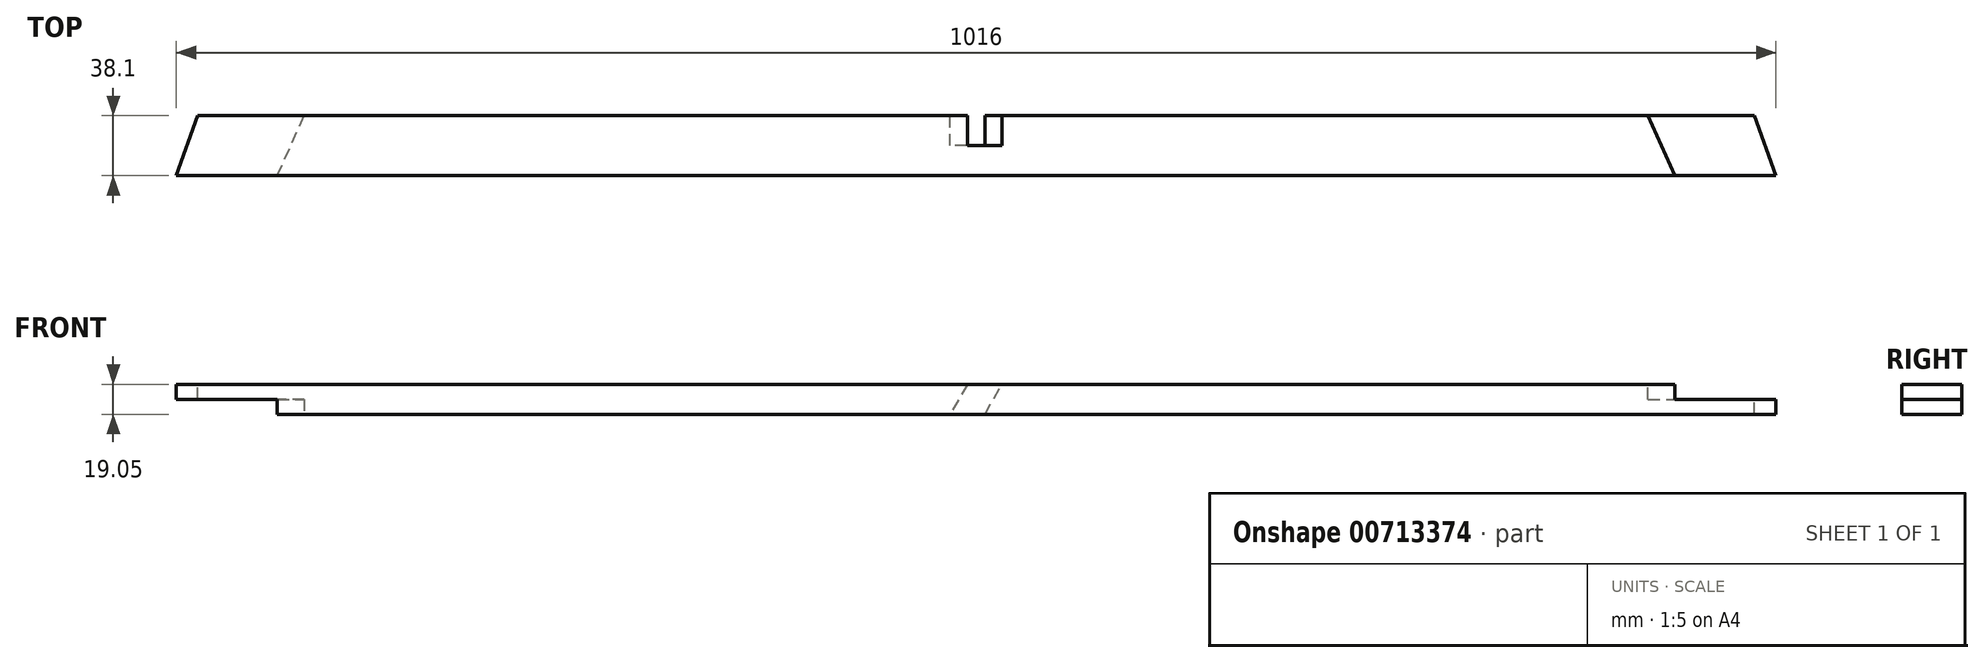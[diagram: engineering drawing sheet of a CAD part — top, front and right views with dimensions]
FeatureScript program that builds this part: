
annotation { "Feature Type Name" : "Feature", "Feature Type Description" : "" }
export const myFeature = defineFeature(function(context is Context, id is Id, definition is map)
    precondition{}
    {
        {
            var Q0;
            Q0=qCreatedBy(makeId("Front.planeOp"),FACE);
            var sketch = newSketch(context, id + "F0", { "sketchPlane" : qUnion([Q0])});
            skLineSegment(sketch, "E0.bottom", {"start": v(0, 0) * mm, "end": v(-1016, 0) * mm});
            skLineSegment(sketch, "E0.top", {"start": v(0, 19.05) * mm, "end": v(-1016, 19.05) * mm});
            skLineSegment(sketch, "E0.left", {"start": v(0, 0) * mm, "end": v(0, 19.05) * mm});
            skLineSegment(sketch, "E0.right", {"start": v(-1016, 0) * mm, "end": v(-1016, 19.05) * mm});
            skSolve(sketch);
        }
        {
            var Q0;
            Q0 = qSketchRegion(id + "F0", true);
            extrude(context, id + "F1", {"entities" : qUnion([Q0]), "depth" : 38.1 * mm, "offsetDistance" : 25.4 * mm});
        }
        {
            var Q0;
            Q0=makeQuery(id+"F1.opExtrude","SWEPT_FACE",FACE,{"disambiguationData":[OSD([sQuery(id+"F0.wireOp",EDGE,"E0.top")])]});
            var sketch = newSketch(context, id + "F2", { "sketchPlane" : qUnion([Q0])});
            skLineSegment(sketch, "E1", {"start": v(-1016, -38.1) * mm, "end": v(-1002.38, 0) * mm});
            skLineSegment(sketch, "E2", {"start": v(-1002.38, 0) * mm, "end": v(-1016, 0) * mm});
            skLineSegment(sketch, "E3", {"start": v(-1016, 0) * mm, "end": v(-1016, -38.1) * mm});
            skSolve(sketch);
        }
        {
            var Q0;
            Q0 = qSketchRegion(id + "F2", true);
            extrude(context, id + "F3", {"entities" : qUnion([Q0]), "operationType" : NewBodyOperationType.REMOVE, "oppositeDirection" : true, "depth" : 50.8 * mm, "offsetDistance" : 25.4 * mm});
        }
        {
            var Q0;
            Q0=makeQuery(id+"F1.opExtrude","SWEPT_FACE",FACE,{"disambiguationData":[OSD([sQuery(id+"F0.wireOp",EDGE,"E0.top")])]});
            var sketch = newSketch(context, id + "F4", { "sketchPlane" : qUnion([Q0])});
            skLineSegment(sketch, "E4", {"start": v(0, -38.1) * mm, "end": v(-13.62, 0) * mm});
            skLineSegment(sketch, "E5", {"start": v(-13.62, 0) * mm, "end": v(0, 0) * mm});
            skLineSegment(sketch, "E6", {"start": v(0, 0) * mm, "end": v(0, -38.1) * mm});
            skSolve(sketch);
        }
        {
            var Q0;
            Q0 = qSketchRegion(id + "F4", true);
            extrude(context, id + "F5", {"entities" : qUnion([Q0]), "operationType" : NewBodyOperationType.REMOVE, "oppositeDirection" : true, "depth" : 76.2 * mm, "offsetDistance" : 25.4 * mm});
        }
        {
            var Q0;
            Q0=makeQuery(id+"F3.boolean.opBoolean","COPY",FACE,{"derivedFrom":makeQuery(id+"F3.opExtrude","SWEPT_FACE",FACE,{"disambiguationData":[OSD([sQuery(id+"F2.wireOp",EDGE,"E1")])]})});
            var sketch = newSketch(context, id + "F6", { "sketchPlane" : qUnion([Q0])});
            skLineSegment(sketch, "E7", {"start": v(258.73, 0) * mm, "end": v(377.94, 0) * mm});
            skLineSegment(sketch, "E8", {"start": v(377.94, 9.53) * mm, "end": v(377.94, 0) * mm});
            skLineSegment(sketch, "E9", {"start": v(377.94, 0) * mm, "end": v(377.94, 9.53) * mm, "construction": true});
            skLineSegment(sketch, "E10", {"start": v(377.94, 9.53) * mm, "end": v(252.78, 9.53) * mm});
            skLineSegment(sketch, "E11", {"start": v(258.73, 0) * mm, "end": v(252.78, 9.53) * mm});
            skSolve(sketch);
        }
        {
            var Q0;
            Q0 = qSketchRegion(id + "F6", true);
            extrude(context, id + "F7", {"entities" : qUnion([Q0]), "operationType" : NewBodyOperationType.REMOVE, "oppositeDirection" : true, "depth" : 60.32 * mm, "offsetDistance" : 25.4 * mm});
        }
        {
            var Q0;
            Q0=makeQuery(id+"F1.opExtrude","SWEPT_FACE",FACE,{"disambiguationData":[OSD([sQuery(id+"F0.wireOp",EDGE,"E0.bottom")])]});
            var sketch = newSketch(context, id + "F8", { "sketchPlane" : qUnion([Q0])});
            skLineSegment(sketch, "E12", {"start": v(-951.93, 0) * mm, "end": v(-951.93, 38.1) * mm});
            skLineSegment(sketch, "E13", {"start": v(-951.93, 0) * mm, "end": v(-934.76, 0) * mm});
            skLineSegment(sketch, "E14", {"start": v(-951.93, 38.1) * mm, "end": v(-934.76, 0) * mm});
            skSolve(sketch);
        }
        {
            var Q0;
            Q0 = qSketchRegion(id + "F8", true);
            extrude(context, id + "F9", {"entities" : qUnion([Q0]), "operationType" : NewBodyOperationType.REMOVE, "oppositeDirection" : true, "depth" : 9.52 * mm, "offsetDistance" : 25.4 * mm});
        }
        {
            var Q0;
            Q0=makeQuery(id+"F5.boolean.opBoolean","COPY",FACE,{"derivedFrom":makeQuery(id+"F5.opExtrude","SWEPT_FACE",FACE,{"disambiguationData":[OSD([sQuery(id+"F4.wireOp",EDGE,"E4")])]})});
            var sketch = newSketch(context, id + "F10", { "sketchPlane" : qUnion([Q0])});
            skLineSegment(sketch, "E15", {"start": v(-35.88, 19.05) * mm, "end": v(-35.88, 0) * mm, "construction": true});
            skLineSegment(sketch, "E16", {"start": v(-35.88, 9.52) * mm, "end": v(45.27, 9.52) * mm});
            skLineSegment(sketch, "E17", {"start": v(-35.88, 19.05) * mm, "end": v(-35.88, 9.52) * mm});
            skLineSegment(sketch, "E18", {"start": v(-35.88, 19.05) * mm, "end": v(45.63, 19.05) * mm});
            skLineSegment(sketch, "E19", {"start": v(45.63, 19.05) * mm, "end": v(45.27, 9.52) * mm});
            skSolve(sketch);
        }
        {
            var Q0;
            Q0 = qSketchRegion(id + "F10", true);
            extrude(context, id + "F11", {"entities" : qUnion([Q0]), "operationType" : NewBodyOperationType.REMOVE, "oppositeDirection" : true, "depth" : 60.32 * mm, "offsetDistance" : 25.4 * mm});
        }
        {
            var Q0;
            Q0=makeQuery(id+"F1.opExtrude","CAP_FACE",FACE,{"disambiguationData":[OSD([sQuery(id+"F0.wireOp",EDGE,"E0.bottom"),sQuery(id+"F0.wireOp",EDGE,"E0.top"),sQuery(id+"F0.wireOp",EDGE,"E0.left"),sQuery(id+"F0.wireOp",EDGE,"E0.right")])],"isStart":true});
            var sketch = newSketch(context, id + "F12", { "sketchPlane" : qUnion([Q0])});
            skLineSegment(sketch, "E20", {"start": v(513.5, 19.05) * mm, "end": v(524.5, 0) * mm});
            skLineSegment(sketch, "E21", {"start": v(502.5, 0) * mm, "end": v(491.5, 19.05) * mm});
            skLineSegment(sketch, "E22", {"start": v(513.5, 19.05) * mm, "end": v(491.5, 19.05) * mm});
            skLineSegment(sketch, "E23", {"start": v(502.5, 0) * mm, "end": v(524.5, 0) * mm});
            skPoint(sketch, "E24.endSnap0", {"position": v(540.03, 19.05) * mm});
            skLineSegment(sketch, "E25", {"start": v(1002.38, 9.52) * mm, "end": v(13.62, 9.53) * mm, "construction": true});
            skLineSegment(sketch, "E26", {"start": v(508, 9.52) * mm, "end": v(508, 19.05) * mm, "construction": true});
            skLineSegment(sketch, "E27", {"start": v(519, 9.52) * mm, "end": v(497, 9.52) * mm, "construction": true});
            skLineSegment(sketch, "E28", {"start": v(497, 9.52) * mm, "end": v(508, 9.52) * mm, "construction": true});
            skSolve(sketch);
        }
        {
            var Q0;
            Q0 = qSketchRegion(id + "F12", true);
            extrude(context, id + "F13", {"entities" : qUnion([Q0]), "operationType" : NewBodyOperationType.REMOVE, "oppositeDirection" : true, "depth" : 19.05 * mm, "offsetDistance" : 25.4 * mm});
        }
        {
            var Q0;
            Q0=makeQuery(id+"F1.opExtrude","SWEPT_FACE",FACE,{"disambiguationData":[OSD([sQuery(id+"F0.wireOp",EDGE,"E0.top")])]});
            var sketch = newSketch(context, id + "F14", { "sketchPlane" : qUnion([Q0])});
            skLineSegment(sketch, "E29", {"start": v(-81.24, 0) * mm, "end": v(-64.07, -38.1) * mm});
            skLineSegment(sketch, "E30", {"start": v(-64.07, 0) * mm, "end": v(-81.24, 0) * mm});
            skLineSegment(sketch, "E31", {"start": v(-64.07, -38.1) * mm, "end": v(-64.07, 0) * mm});
            skSolve(sketch);
        }
        {
            var Q0;
            Q0 = qSketchRegion(id + "F14", true);
            extrude(context, id + "F15", {"entities" : qUnion([Q0]), "operationType" : NewBodyOperationType.REMOVE, "oppositeDirection" : true, "depth" : 9.52 * mm, "offsetDistance" : 25.4 * mm});
        }
    });
